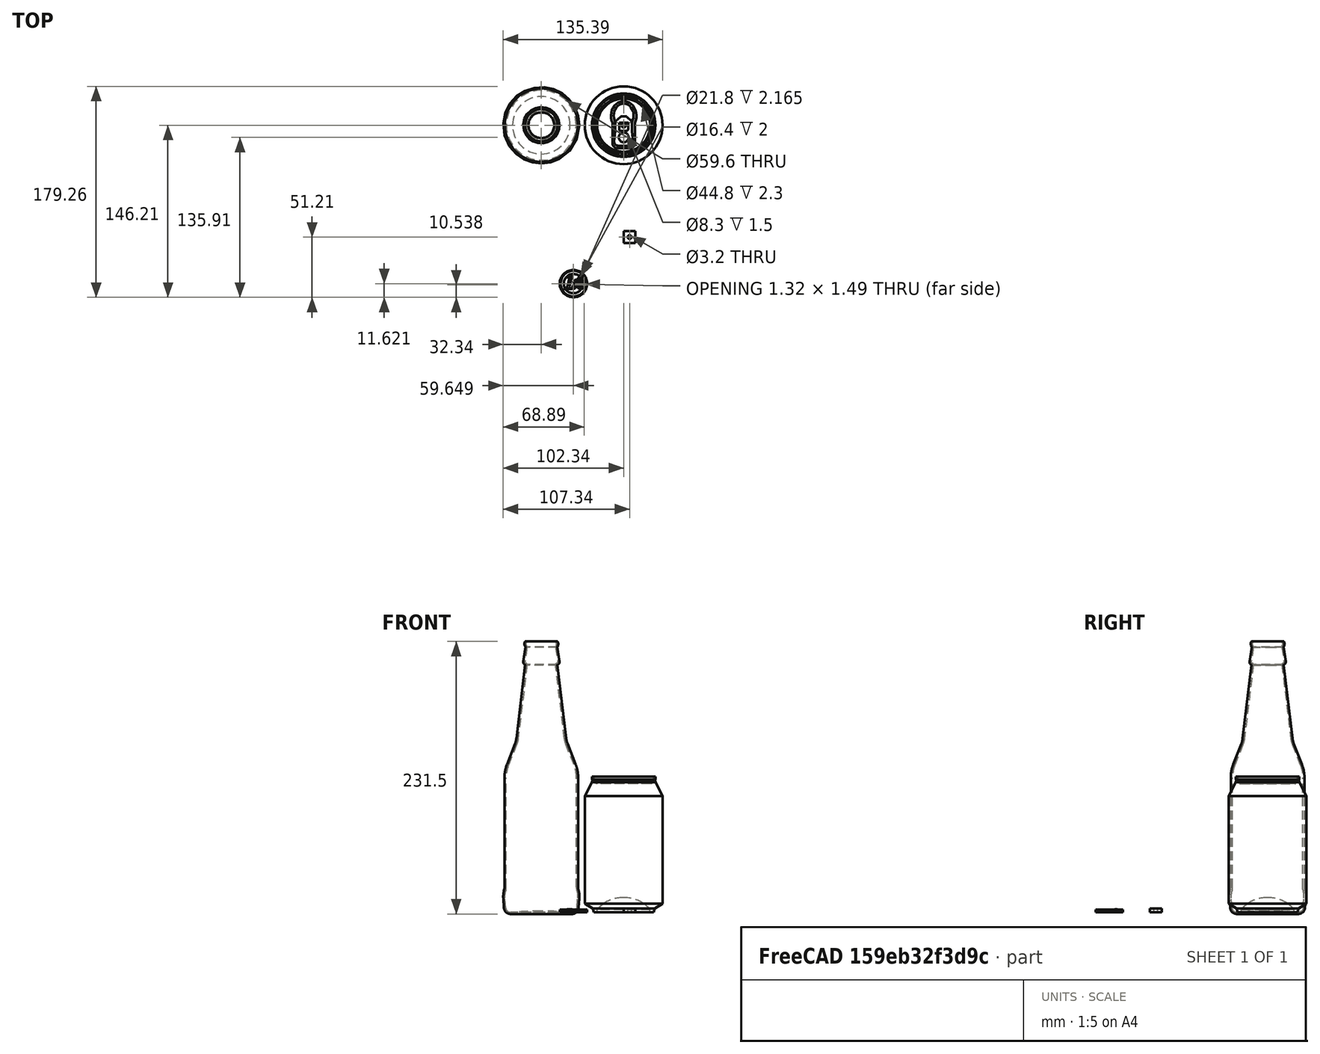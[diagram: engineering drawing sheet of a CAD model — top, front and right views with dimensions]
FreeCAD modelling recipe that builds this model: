
FCSTD DOCUMENT  (FreeCAD 0.16R6707 (Git))
Label: 01-ejemplo-taladro-cubo
License: All rights reserved
LicenseURL: http://en.wikipedia.org/wiki/All_rights_reserved
objects: Part::Feature×3, Part::Box×1, Part::Cylinder×1, Part::Cut×1
note: 6 computed .brp shape members not serialized (recipe doc carries the construction recipe); baked Part::Feature solids carry a one-line shape summary decoded from their .brp

FEATURE [Part::Feature] Compound001  label="Euro-coin"
  Placement = pos=(-42.6911,-34.9892,0) rot=(0,0,1;0rad)
  shape: bbox 23.25 x 23.25 x 2.414 mm, 903 faces, 22 solids (baked)
FEATURE [Part::Feature] Thickness001  label="Bottle"
  Placement = pos=(-70,100,0) rot=(0,0,1;0rad)
  shape: bbox 71.75 x 74.3 x 235 mm, 40 faces (baked)
FEATURE [Part::Feature] Fusion001  label="Can"
  Placement = pos=(0,100,0) rot=(0,0,1;0rad)
  shape: bbox 66.1 x 66.1 x 115.2 mm, 53 faces (baked)
FEATURE [Part::Box] Box  label="Cubo"
  Height = 3
  Length = 10
  Width = 10
FEATURE [Part::Cylinder] Cylinder  label="Cilindro"
  Angle = 360
  Height = 10
  Placement = pos=(5,5,-4) rot=(0,0,1;0rad)
  Radius = 1.6
FEATURE [Part::Cut] Cut  label="Pieza-con-taladro"
  Base = -> Box
  Tool = -> Cylinder
